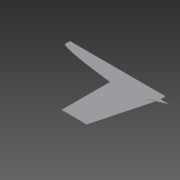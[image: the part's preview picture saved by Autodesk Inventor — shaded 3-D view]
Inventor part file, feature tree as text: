
AUTODESK INVENTOR PART (.ipt)
format: ipt  version: 2014 SP1 (Build 180222100, 222)  size: 112,128 bytes
history: native  units: mm
features: chamfer x4, fillet x2, extrude x1, sketch x1
ambient origin geometry x8: Origin, YZ Plane, XZ Plane, XY Plane, X Axis, Y Axis, Z Axis, Center Point
bodies: Solid1 (feature_tree)
feature tree (8):
  extrude  "Extrusion1"  Depth=2.5mm TaperAngle=0.0deg
  fillet  "Fillet1"  Radius=2.5mm
  chamfer  "Chamfer1"  Distance=120.0mm
  chamfer  "Chamfer2"  Distance=40.0mm
  fillet  "Fillet4"  Radius=30.0mm
  chamfer  "Chamfer3"  Distance=30.0mm
  chamfer  "Chamfer4"  Distance=2.5mm
  sketch  "Sketch1"  dims[d5=25.0mm d6=5.0mm d7=0.0mm d8=2.5mm d21=120.0mm d22=40.0mm d25=30.0mm d26=2.0mm d27=0.872665mm d28=30.0mm d29=2.0mm d30=0.698132mm d31=2.5mm d32=30.0mm d33=2.0mm d34=0.698132mm d35=30.0mm d36=2.0mm d37=0.698132mm]
